# Revit family: ShowerBase_ProBaseII_NobleCompany
name_source: partatom
category: Specialty Equipment
revit_build: Autodesk Revit 2015 (Build: 20140606_1530(x64)
units: mm (PartAtom-declared; Revit-internal decimal feet)

## types (4) — shared parameters
Assembly Code = D2030300
Base = Polypropylene - High Strength
Building Codes = http://www.noblecompany.com
Default Elevation = 0"
Description = Noble Pro Base II Shower Base Kit
Drain Hole Diameter = 3"
Drain Width = 4 1/2"
DrainLoc = 6 3/4"
Hang = 1/8"
Height = 2 15/32"
Installation-Fabrication = http://www.noblecompany.com
Keynote = 09 30 13.A3
Manufacturer = Noble Company
Manufacturer Fax = 231-799-8850
Product Data = http://www.noblecompany.com
Product Properties = http://www.noblecompany.com
URL = www.noblecompany.com
Width = 64 1/2"

## per-type parameters (varying)
| type | Cut_Head | Depth | Drain Length | Flush to Wall | Model |
| 32x60 Flush to Wall | 4 1/2" | 32" | 24" | Yes | Pro Base II 3260 |
| 32x60 Offset Drain | 0" | 32" | 24" | No | Pro Base II 3260 |
| 64x64 Flush to Wall | 4 1/2" | 64" | 60" | Yes | Pro Base II 6464 |
| 64x64 Offset Drain | 0" | 64" | 60" | No | Pro Base II 6464 |

## geometry (parser evidence)
native form markers: Sweep x3
no freeform markers — native parametric forms only
